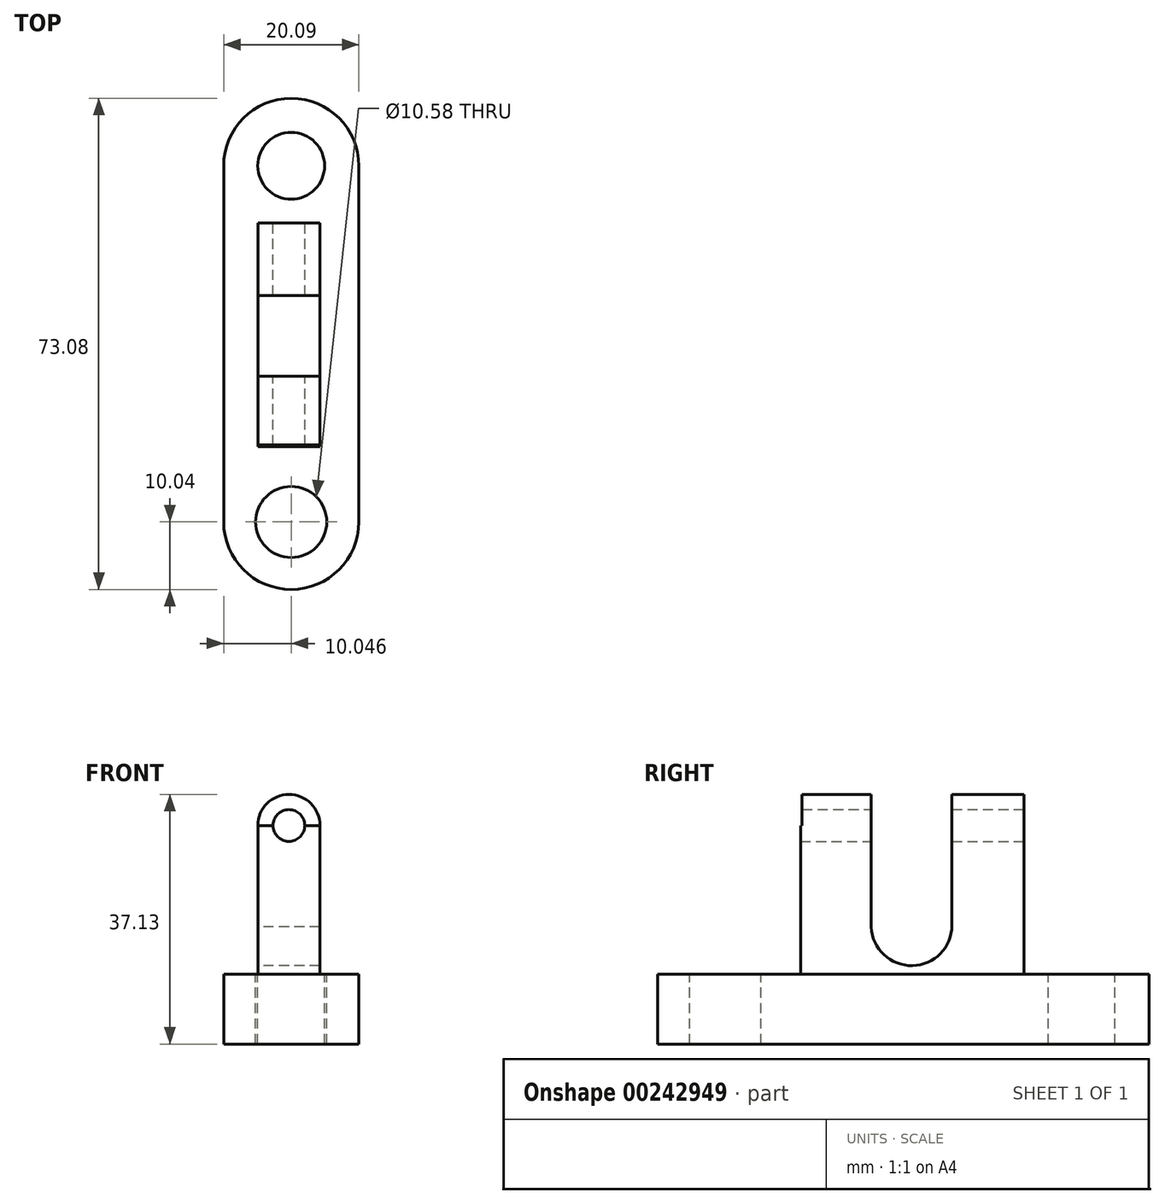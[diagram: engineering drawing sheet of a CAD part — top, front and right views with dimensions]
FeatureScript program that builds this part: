
annotation { "Feature Type Name" : "Feature", "Feature Type Description" : "" }
export const myFeature = defineFeature(function(context is Context, id is Id, definition is map)
    precondition{}
    {
        {
            var Q0;
            Q0=qCreatedBy(makeId("Top.planeOp"),FACE);
            var sketch = newSketch(context, id + "F0", { "sketchPlane" : qUnion([Q0])});
            skLineSegment(sketch, "E0.left", {"start": v(0, 0) * mm, "end": v(0, 53) * mm});
            skLineSegment(sketch, "E0.right", {"start": v(-20.09, 0) * mm, "end": v(-20.09, 53) * mm});
            skArc(sketch, "E1", {"start": v(-20.09, 53) * mm, "mid": v(-10.04, 63.04) * mm, "end": v(0, 53) * mm});
            skArc(sketch, "E2", {"start": v(-20.09, 0) * mm, "mid": v(-10.04, -10.04) * mm, "end": v(0, 0) * mm});
            skSolve(sketch);
        }
        {
            var Q0;
            Q0=makeQuery(id+"F0.imprint","IMPRINT",FACE,{"disambiguationData":[TD([[makeQuery(id+"F0.imprint","IMPRINT",EDGE,{"derivedFrom":sQuery(id+"F0.wireOp",EDGE,"E0.left")}),1.0]])]});
            extrude(context, id + "F1", {"entities" : qUnion([Q0]), "depth" : 10.4 * mm});
        }
        {
            var Q0;
            Q0=makeQuery(id+"F1.opExtrude","CAP_FACE",FACE,{"disambiguationData":[OSD([sQuery(id+"F0.wireOp",EDGE,"E0.left"),sQuery(id+"F0.wireOp",EDGE,"E0.right"),sQuery(id+"F0.wireOp",EDGE,"E1"),sQuery(id+"F0.wireOp",EDGE,"E2")])],"isStart":false});
            var sketch = newSketch(context, id + "F2", { "sketchPlane" : qUnion([Q0])});
            skLineSegment(sketch, "E3.bottom", {"start": v(-5.77, 44.45) * mm, "end": v(-15, 44.45) * mm});
            skLineSegment(sketch, "E3.top", {"start": v(-5.77, 11.2) * mm, "end": v(-15, 11.2) * mm});
            skLineSegment(sketch, "E3.left", {"start": v(-5.77, 44.45) * mm, "end": v(-5.77, 11.2) * mm});
            skLineSegment(sketch, "E3.right", {"start": v(-15, 44.45) * mm, "end": v(-15, 11.2) * mm});
            skPoint(sketch, "E3.middle", {"position": v(-10.4, 27.82) * mm});
            skSolve(sketch);
        }
        {
            var Q0;
            Q0=makeQuery(id+"F2.imprint","IMPRINT",FACE,{"disambiguationData":[TD([[makeQuery(id+"F2.imprint","IMPRINT",EDGE,{"derivedFrom":sQuery(id+"F2.wireOp",EDGE,"E3.bottom")}),1.0]])]});
            extrude(context, id + "F3", {"entities" : qUnion([Q0]), "operationType" : NewBodyOperationType.ADD, "depth" : 22.1 * mm});
        }
        {
            var Q0;
            Q0=makeQuery(id+"F3.opExtrude","SWEPT_FACE",FACE,{"disambiguationData":[OSD([sQuery(id+"F2.wireOp",EDGE,"E3.right")])]});
            var sketch = newSketch(context, id + "F4", { "sketchPlane" : qUnion([Q0])});
            skLineSegment(sketch, "E4", {"start": v(-33.71, 32.51) * mm, "end": v(-33.71, 17.66) * mm});
            skLineSegment(sketch, "E5", {"start": v(-21.7, 32.51) * mm, "end": v(-21.7, 17.43) * mm});
            skArc(sketch, "E6", {"start": v(-33.71, 17.66) * mm, "mid": v(-27.82, 11.66) * mm, "end": v(-21.7, 17.43) * mm});
            skLineSegment(sketch, "E7", {"start": v(-33.71, 32.51) * mm, "end": v(-21.7, 32.51) * mm});
            skSolve(sketch);
        }
        {
            var Q0;
            Q0=makeQuery(id+"F4.imprint","IMPRINT",FACE,{"disambiguationData":[TD([[makeQuery(id+"F4.imprint","IMPRINT",EDGE,{"derivedFrom":sQuery(id+"F4.wireOp",EDGE,"E4")}),1.0]])]});
            extrude(context, id + "F5", {"entities" : qUnion([Q0]), "operationType" : NewBodyOperationType.REMOVE, "oppositeDirection" : true, "depth" : 59.94 * mm});
        }
        {
            var Q0;
            Q0=makeQuery(id+"F3.opExtrude","SWEPT_FACE",FACE,{"disambiguationData":[OSD([sQuery(id+"F2.wireOp",EDGE,"E3.bottom")])]});
            var sketch = newSketch(context, id + "F6", { "sketchPlane" : qUnion([Q0])});
            skArc(sketch, "E8", {"start": v(15, 32.51) * mm, "mid": v(10.4, 37.13) * mm, "end": v(5.77, 32.51) * mm});
            skSolve(sketch);
        }
        {
            var Q0;
            Q0=makeQuery(id+"F6.imprint","IMPRINT",FACE,{"disambiguationData":[TD([[makeQuery(id+"F6.imprint","IMPRINT",EDGE,{"derivedFrom":sQuery(id+"F6.wireOp",EDGE,"E8")}),1.0]])]});
            extrude(context, id + "F7", {"entities" : qUnion([Q0]), "operationType" : NewBodyOperationType.ADD, "oppositeDirection" : true, "depth" : 33.02 * mm});
        }
        {
            var Q0;
            {var subQ0=sQuery(id+"F2.wireOp",EDGE,"E3.bottom");Q0=makeQuery(id+"F7.boolean.opBoolean","MERGE",FACE,{"derivedFrom":[makeQuery(id+"F3.opExtrude","SWEPT_FACE",FACE,{"disambiguationData":[OSD([subQ0])]}),makeQuery(id+"F7.opExtrude","CAP_FACE",FACE,{"disambiguationData":[OSD([subQ0,sQuery(id+"F6.wireOp",EDGE,"E8")])],"isStart":true})]});}
            var sketch = newSketch(context, id + "F8", { "sketchPlane" : qUnion([Q0])});
            skCircle(sketch, "E9", {"center": v(10.4, 32.51) * mm, "radius": 2.36 * mm});
            skSolve(sketch);
        }
        {
            var Q0;
            Q0=makeQuery(id+"F8.imprint","IMPRINT",FACE,{"disambiguationData":[TD([[makeQuery(id+"F8.imprint","IMPRINT",EDGE,{"derivedFrom":sQuery(id+"F8.wireOp",EDGE,"E9")}),1.0]])]});
            extrude(context, id + "F9", {"entities" : qUnion([Q0]), "operationType" : NewBodyOperationType.REMOVE, "oppositeDirection" : true, "depth" : 56.9 * mm});
        }
        {
            var Q0;
            Q0=makeQuery(id+"F1.opExtrude","CAP_FACE",FACE,{"disambiguationData":[OSD([sQuery(id+"F0.wireOp",EDGE,"E0.left"),sQuery(id+"F0.wireOp",EDGE,"E0.right"),sQuery(id+"F0.wireOp",EDGE,"E1"),sQuery(id+"F0.wireOp",EDGE,"E2")])],"isStart":false});
            var sketch = newSketch(context, id + "F10", { "sketchPlane" : qUnion([Q0])});
            skCircle(sketch, "E10", {"center": v(-10.04, 53) * mm, "radius": 4.97 * mm});
            skCircle(sketch, "E11", {"center": v(-10.04, 0) * mm, "radius": 5.29 * mm});
            skSolve(sketch);
        }
        {
            var Q0;
            Q0=makeQuery(id+"F10.imprint","IMPRINT",FACE,{"disambiguationData":[TD([[makeQuery(id+"F10.imprint","IMPRINT",EDGE,{"derivedFrom":sQuery(id+"F10.wireOp",EDGE,"E10")}),1.0]])]});
            var Q1;
            Q1=makeQuery(id+"F10.imprint","IMPRINT",FACE,{"disambiguationData":[TD([[makeQuery(id+"F10.imprint","IMPRINT",EDGE,{"derivedFrom":sQuery(id+"F10.wireOp",EDGE,"E11")}),1.0]])]});
            extrude(context, id + "F11", {"entities" : qUnion([Q0, Q1]), "operationType" : NewBodyOperationType.REMOVE, "oppositeDirection" : true, "depth" : 52.32 * mm});
        }
        {
            var Q0;
            Q0=makeQuery(id+"F3.opExtrude","SWEPT_FACE",FACE,{"disambiguationData":[OSD([sQuery(id+"F2.wireOp",EDGE,"E3.left")])]});
            var sketch = newSketch(context, id + "F12", { "sketchPlane" : qUnion([Q0])});
            skLineSegment(sketch, "E12.bottom", {"start": v(21.7, 22.98) * mm, "end": v(33.71, 22.98) * mm});
            skLineSegment(sketch, "E12.top", {"start": v(21.7, 43.53) * mm, "end": v(33.71, 43.53) * mm});
            skLineSegment(sketch, "E12.left", {"start": v(21.7, 22.98) * mm, "end": v(21.7, 43.53) * mm});
            skLineSegment(sketch, "E12.right", {"start": v(33.71, 22.98) * mm, "end": v(33.71, 43.53) * mm});
            skSolve(sketch);
        }
        {
            var Q0;
            Q0=qSketchRegion(id+"F12",true);
            extrude(context, id + "F13", {"entities" : qUnion([Q0]), "operationType" : NewBodyOperationType.REMOVE, "oppositeDirection" : true, "depth" : 54.36 * mm});
        }
    });
